# Revit family: LeL OLO 1.0
name_source: partatom
category: Lighting Fixtures
units: mm (PartAtom-declared; Revit-internal decimal feet)

## family parameters
Always vertical = No
Cut with Voids When Loaded = No
Light Source = No
OmniClass Number = 23.80.70.00
OmniClass Title = Lighting
Part Type = Normal
Room Calculation Point = No
Round Connector Dimension = Use Diameter
Shared = No
Work Plane-Based = Yes

## types (8) — shared parameters
CCT = 3000 K
CRI = CRI80
Default Elevation = 1219 mm
Description = Outdoor Bollard
Lamp = LED
Manufacturer = L&L Luce&Light srl
Model = LL10
Rated Power supply = 230 V
URL = www.lucelight.it/en/prodotto.php/195007

## per-type parameters (varying)
| type | Apparent Load | Lumen Output | Photometry | Wattage |
| 1.0 A 14W 230Vac | 14 VA | 1461 lm | OL1 Light source : 1.0 A 14W 230Vac | 14 W |
| 1.0 A 14W DALI full | 14 VA | 1285 lm | OL1 Light source : 1.0 A 14W DALI full | 14 W |
| 1.0 A 14W DALI long | 14 VA | 662 lm | OL1 Light source : 1.0 A 14W DALI long | 14 W |
| 1.0 A 14W DALI short | 14 VA | 652 lm | OL1 Light source : 1.0 A 14W DALI short | 14 W |
| 1.0 R 19W 230Vac | 19 VA | 2057 lm | OL1 Light source : 1.0 R 19W 230Vac | 19 W |
| 1.0 R 19W DALI full | 19 VA | 1969 lm | OL1 Light source : 1.0 R 19W DALI full | 19 W |
| 1.0 R 19W DALI long | 19 VA | 1338 lm | OL1 Light source : 1.0 R 19W DALI long | 19 W |
| 1.0 R 19W DALI short | 19 VA | 687 lm | OL1 Light source : 1.0 R 19W DALI short | 19 W |

## geometry (parser evidence)
native form markers: Sweep x3
no freeform markers — native parametric forms only
